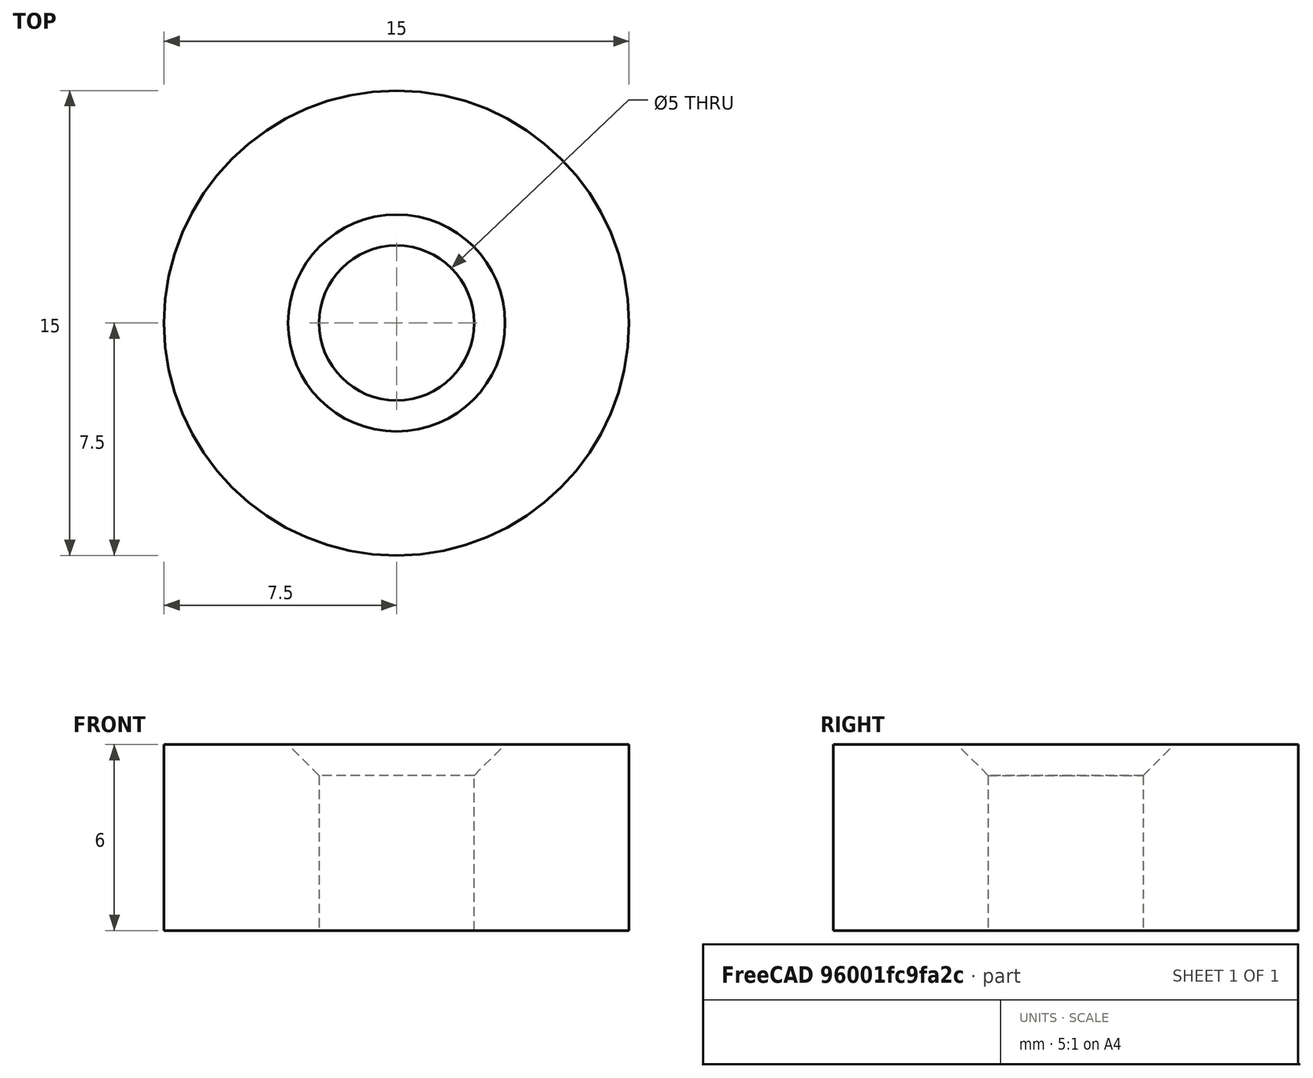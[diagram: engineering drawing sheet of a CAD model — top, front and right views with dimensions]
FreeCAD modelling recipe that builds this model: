
FCSTD DOCUMENT  (FreeCAD 0.19R24276 (Git))
Label: Z_Belt_tension_axis_fix_v1
License: All rights reserved
LicenseURL: http://en.wikipedia.org/wiki/All_rights_reserved
objects: Sketcher::SketchObject×1, PartDesign::Pad×1, PartDesign::Chamfer×1, PartDesign::Body×1
note: 6 computed .brp shape members not serialized (recipe doc carries the construction recipe); baked Part::Feature solids carry a one-line shape summary decoded from their .brp

FEATURE [Sketcher::SketchObject] Sketch
  FullyConstrained = true
  MapMode = 5
  Support = -> [XY_Plane]
  sketch-geometry (2):
    g0: Circle CenterX=0 CenterY=0 CenterZ=0 NormalX=0 NormalY=0 NormalZ=1 AngleXU=0 Radius=2.5
    g1: Circle CenterX=0 CenterY=0 CenterZ=0 NormalX=0 NormalY=0 NormalZ=1 AngleXU=0 Radius=7.5
  constraints (4):
    c: Coincident(g0,g-1)
    c: Coincident(g1,g0)
    c: Diameter(g0) = 5
    c: Diameter(g1) = 15
FEATURE [PartDesign::Pad] Pad
  Direction = (1,1,1)
  Length = 6
  Length2 = 100
  Profile = -> Sketch
  Type = 0
FEATURE [PartDesign::Chamfer] Chamfer
  Angle = 45
  Base = -> Pad [Edge6]
  BaseFeature = -> Pad
  ChamferType = 0
  FlipDirection = false
  Size = 1
  Size2 = 1
  SupportTransform = false
FEATURE [PartDesign::Body] Body
  Group = -> [Sketch,Pad,Chamfer]
  Origin = -> Origin
  Tip = -> Chamfer
